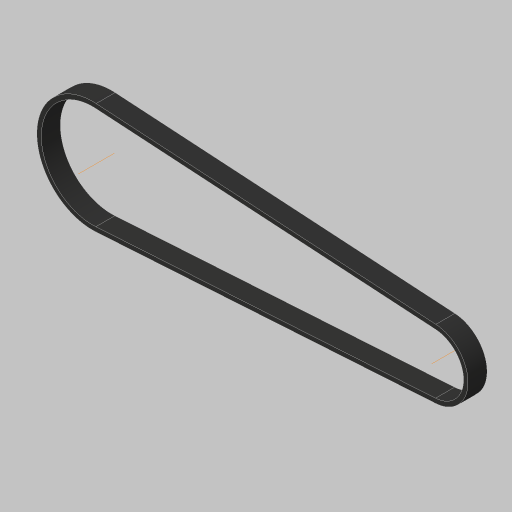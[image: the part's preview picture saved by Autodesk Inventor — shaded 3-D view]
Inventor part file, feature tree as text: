
AUTODESK INVENTOR PART (.ipt)
format: ipt  version: 2023.5 (Build 275446000, 446)  size: 166,912 bytes
history: native  units: in
note: dims shown in document units (in); Inventor stores cm internally (conversion verified against a paired STEP export)
features: sketch x3, extrude x1, other x1, projected_geometry x1
ambient origin geometry x8: Origin, YZ Plane, XZ Plane, XY Plane, X Axis, Y Axis, Z Axis, Center Point
bodies: Body1 (feature_tree)
feature tree (6):
  sketch  "Sketch2"  dims[d0=1.1279in d1=1.8798in]
  extrude  "Extrusion2"  Depth=1.8798in
  sketch  "Sketch5"  dims[d3=3.0709in d5=5.9803in d9=0.0787in d10=0.0598in d11=0.0299in d12=0.0219in d13=0.0219in d14=0.0059in d15=0.0059in d20=0.3346in d21=0.0in d22=0.0787in d23=0.0598in d24=0.0299in d25=0.0219in d26=0.0219in d27=0.0059in d28=0.0059in d29=0.0299in d30=0.0394in d31=0.0787in d32=0.0232in d34=0.0219in d35=0.0in d36=0.0in d37=0.0059in d38=0.0022in d39=0.0022in d40=0.0in d41=0.0in d42=0.0081in d43=0.0081in d44=0.0394in]
  other  "Work Axis1"
  sketch  "Sketch4"  dims[d2=1.7009in]
  projected_geometry  "Projected Loop1"
